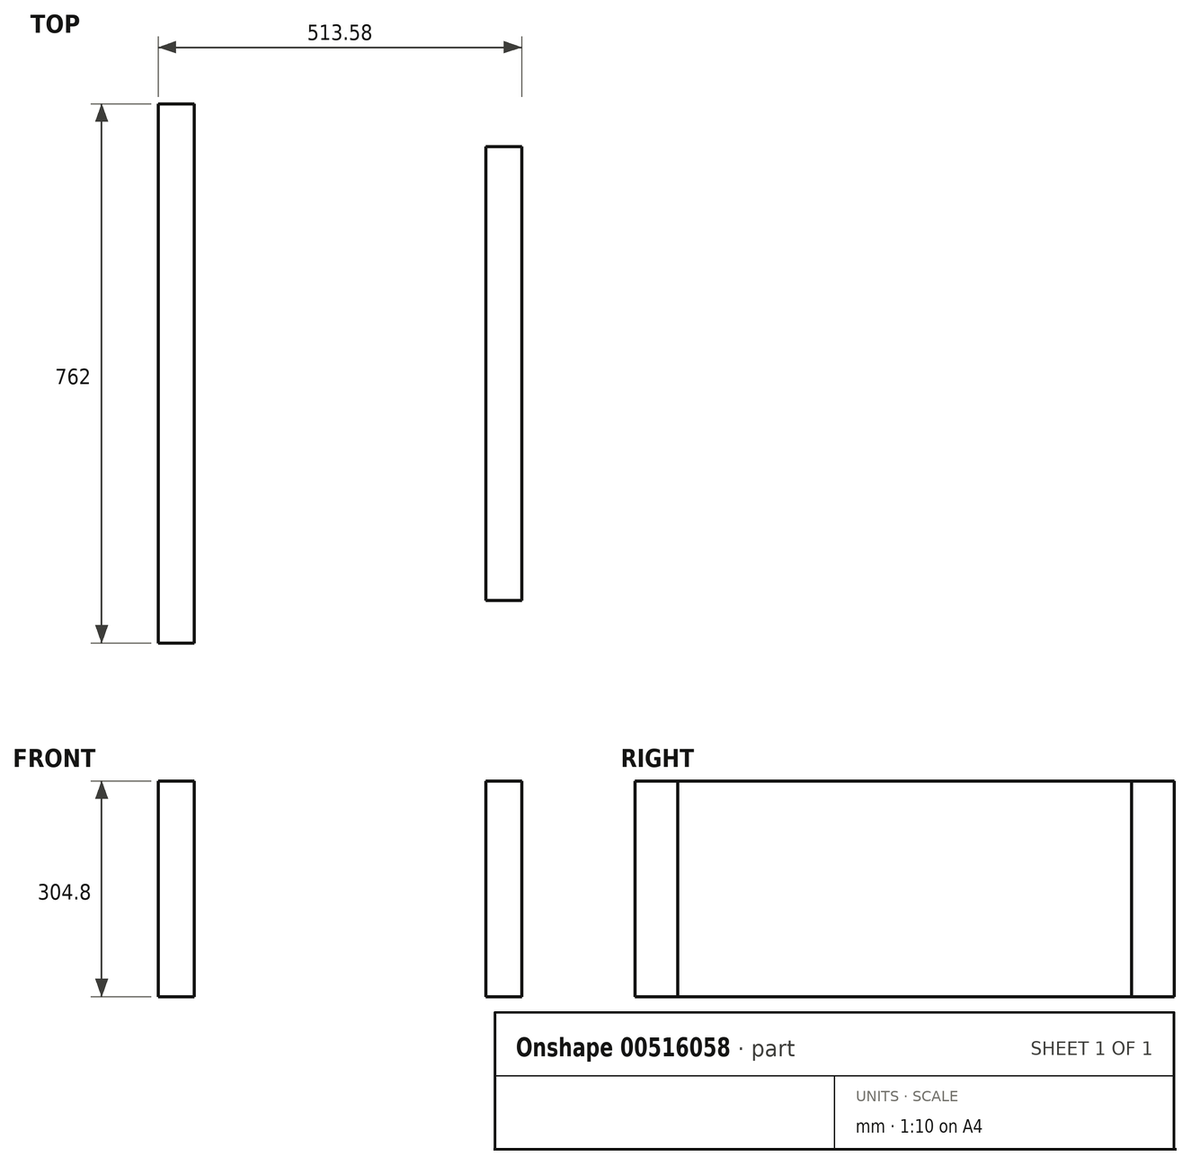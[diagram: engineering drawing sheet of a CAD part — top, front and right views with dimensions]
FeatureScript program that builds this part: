
annotation { "Feature Type Name" : "Feature", "Feature Type Description" : "" }
export const myFeature = defineFeature(function(context is Context, id is Id, definition is map)
    precondition{}
    {
        {
            var Q0;
            Q0=qCreatedBy(makeId("Top.planeOp"),FACE);
            var sketch = newSketch(context, id + "F0", { "sketchPlane" : qUnion([Q0])});
            skLineSegment(sketch, "E0.bottom", {"start": v(25.4, -381) * mm, "end": v(-25.4, -381) * mm});
            skLineSegment(sketch, "E0.top", {"start": v(25.4, 381) * mm, "end": v(-25.4, 381) * mm});
            skLineSegment(sketch, "E0.left", {"start": v(25.4, -381) * mm, "end": v(25.4, 381) * mm});
            skLineSegment(sketch, "E0.right", {"start": v(-25.4, -381) * mm, "end": v(-25.4, 381) * mm});
            skPoint(sketch, "E0.middle", {"position": v(0, 0) * mm});
            skLineSegment(sketch, "E1.bottom", {"start": v(488.18, -320.68) * mm, "end": v(437.38, -320.68) * mm});
            skLineSegment(sketch, "E1.top", {"start": v(488.18, 320.68) * mm, "end": v(437.38, 320.68) * mm});
            skLineSegment(sketch, "E1.left", {"start": v(488.18, -320.68) * mm, "end": v(488.18, 320.67) * mm});
            skLineSegment(sketch, "E1.right", {"start": v(437.38, -320.68) * mm, "end": v(437.38, 320.67) * mm});
            skPoint(sketch, "E1.middle", {"position": v(462.78, 0) * mm});
            skPoint(sketch, "E1.middle.positionSnap0", {"position": v(25.4, 0) * mm});
            skPoint(sketch, "E1.centerSnap0", {"position": v(25.4, 0) * mm});
            skSolve(sketch);
        }
        {
            var Q0;
            Q0=makeQuery(id+"F0.imprint","IMPRINT",FACE,{"disambiguationData":[TD([[makeQuery(id+"F0.imprint","IMPRINT",EDGE,{"derivedFrom":sQuery(id+"F0.wireOp",EDGE,"E0.bottom")}),-1.0]])]});
            var Q1;
            Q1=makeQuery(id+"F0.imprint","IMPRINT",FACE,{"disambiguationData":[TD([[makeQuery(id+"F0.imprint","IMPRINT",EDGE,{"derivedFrom":sQuery(id+"F0.wireOp",EDGE,"E1.bottom")}),-1.0]])]});
            extrude(context, id + "F1", {"entities" : qUnion([Q0, Q1]), "depth" : 304.8 * mm, "offsetDistance" : 25.4 * mm});
        }
    });
